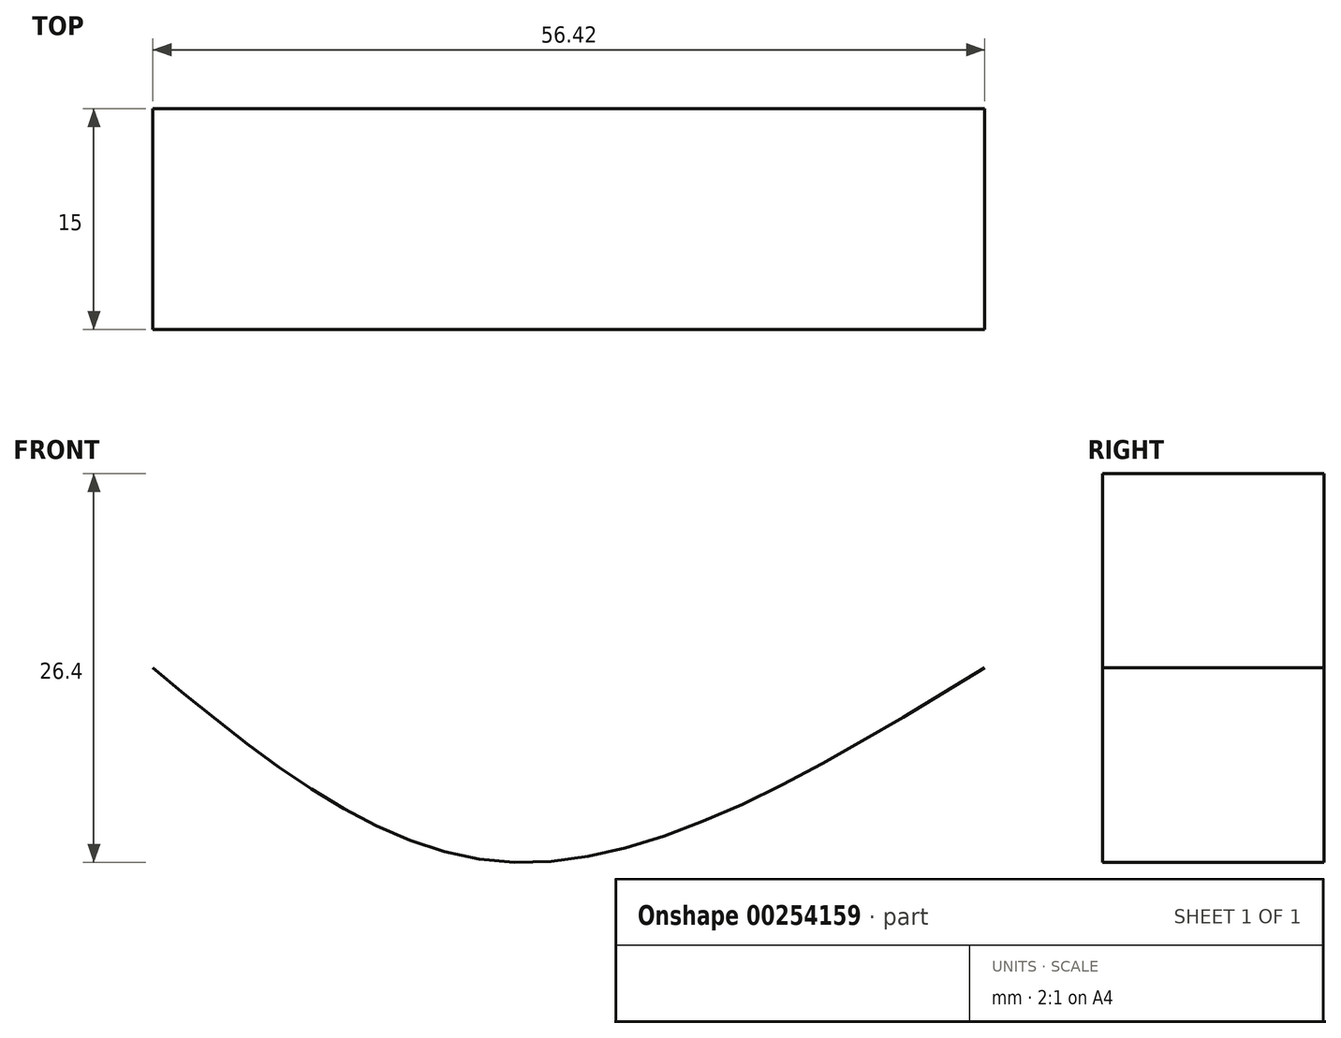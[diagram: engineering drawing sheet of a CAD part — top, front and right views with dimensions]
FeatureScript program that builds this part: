
annotation { "Feature Type Name" : "Feature", "Feature Type Description" : "" }
export const myFeature = defineFeature(function(context is Context, id is Id, definition is map)
    precondition{}
    {
        {
            var Q0;
            Q0=qCreatedBy(makeId("Front.planeOp"),FACE);
            var sketch = newSketch(context, id + "F0", { "sketchPlane" : qUnion([Q0])});
            skLineSegment(sketch, "E0", {"start": v(0, 0) * mm, "end": v(16.75, 0) * mm});
            skFitSpline(sketch, "E1", {"points": [v(16.75, 0) * mm, v(40.8, 13.17) * mm, v(73.17, 0) * mm], "startDerivative": vector(48.9, 40.45) * mm, "endDerivative": vector(63.63, -38.85) * mm});
            skLineSegment(sketch, "E2", {"start": v(73.17, 0) * mm, "end": v(16.75, 0) * mm});
            skFitSpline(sketch, "E3.MirrorCS", {"points": [v(16.75, 0) * mm, v(40.8, -13.17) * mm, v(73.17, 0) * mm], "startDerivative": vector(48.9, -40.45) * mm, "endDerivative": vector(63.63, 38.85) * mm});
            skSolve(sketch);
        }
        {
            var Q0;
            Q0=makeQuery(id+"F0.imprint","IMPRINT",FACE,{"disambiguationData":[TD([[makeQuery(id+"F0.imprint","IMPRINT",EDGE,{"derivedFrom":sQuery(id+"F0.wireOp",EDGE,"E2")}),1.0]])]});
            var Q1;
            Q1=makeQuery(id+"F0.imprint","IMPRINT",FACE,{"disambiguationData":[TD([[makeQuery(id+"F0.imprint","IMPRINT",EDGE,{"derivedFrom":sQuery(id+"F0.wireOp",EDGE,"E1")}),-1.0]])]});
            extrude(context, id + "F1", {"entities" : qUnion([Q0, Q1]), "endBound" : BoundingType.SYMMETRIC, "depth" : 15 * mm});
        }
    });
